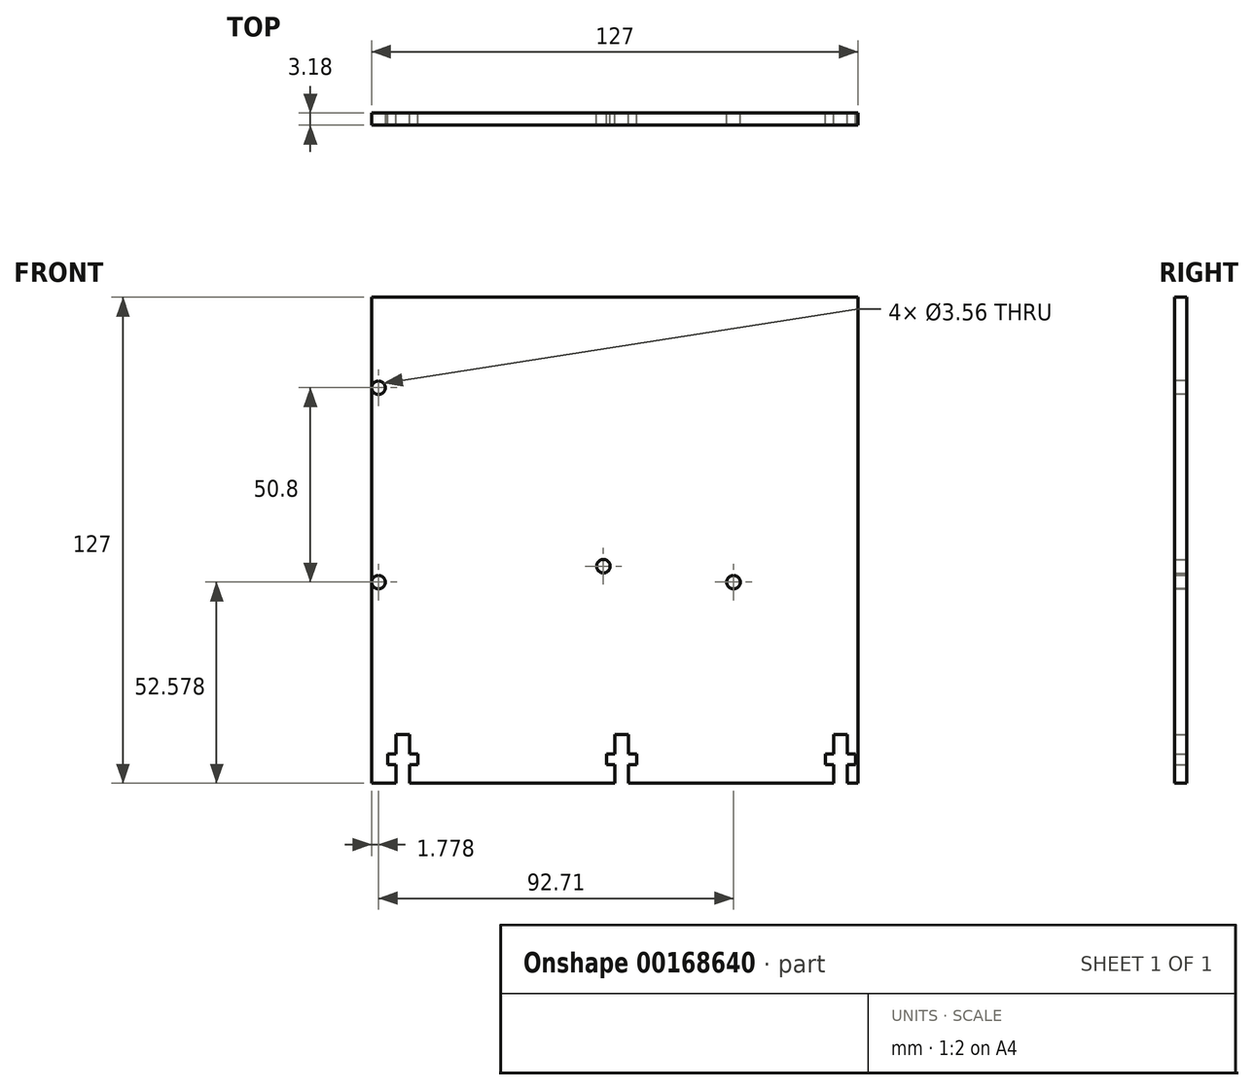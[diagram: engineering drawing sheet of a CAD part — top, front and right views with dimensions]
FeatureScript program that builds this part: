
annotation { "Feature Type Name" : "Feature", "Feature Type Description" : "" }
export const myFeature = defineFeature(function(context is Context, id is Id, definition is map)
    precondition{}
    {
        {
            var Q0;
            Q0=qCreatedBy(makeId("Front.planeOp"),FACE);
            var sketch = newSketch(context, id + "F0", { "sketchPlane" : qUnion([Q0])});
            skLineSegment(sketch, "E0.bottom", {"start": v(63.5, -63.5) * mm, "end": v(-63.5, -63.5) * mm});
            skLineSegment(sketch, "E0.top", {"start": v(63.5, 63.5) * mm, "end": v(-63.5, 63.5) * mm});
            skLineSegment(sketch, "E0.left", {"start": v(63.5, -63.5) * mm, "end": v(63.5, 63.5) * mm});
            skLineSegment(sketch, "E0.right", {"start": v(-63.5, -63.5) * mm, "end": v(-63.5, 63.5) * mm});
            skPoint(sketch, "E0.middle", {"position": v(0, 0) * mm});
            skLineSegment(sketch, "E1", {"start": v(-57.15, -63.5) * mm, "end": v(-57.15, -58.66) * mm});
            skLineSegment(sketch, "E2", {"start": v(-57.15, -58.66) * mm, "end": v(-59.34, -58.66) * mm});
            skLineSegment(sketch, "E3", {"start": v(-59.34, -58.66) * mm, "end": v(-59.34, -55.88) * mm});
            skLineSegment(sketch, "E4", {"start": v(-59.34, -55.88) * mm, "end": v(-57.15, -55.88) * mm});
            skLineSegment(sketch, "E5", {"start": v(-57.15, -55.88) * mm, "end": v(-57.15, -50.8) * mm});
            skLineSegment(sketch, "E6", {"start": v(-57.15, -50.8) * mm, "end": v(-53.6, -50.8) * mm});
            skLineSegment(sketch, "E7", {"start": v(-53.6, -50.8) * mm, "end": v(-53.6, -55.88) * mm});
            skLineSegment(sketch, "E8", {"start": v(-53.6, -55.88) * mm, "end": v(-51.4, -55.88) * mm});
            skLineSegment(sketch, "E9", {"start": v(-51.4, -55.88) * mm, "end": v(-51.4, -58.66) * mm});
            skLineSegment(sketch, "E10", {"start": v(-51.4, -58.66) * mm, "end": v(-53.6, -58.66) * mm});
            skLineSegment(sketch, "E11", {"start": v(-53.6, -58.66) * mm, "end": v(-53.6, -63.5) * mm});
            skLineSegment(sketch, "E12.1.0.0", {"start": v(-2.2, -58.66) * mm, "end": v(-2.2, -55.88) * mm});
            skLineSegment(sketch, "E12.1.0.1", {"start": v(5.75, -58.66) * mm, "end": v(3.56, -58.66) * mm});
            skLineSegment(sketch, "E12.1.0.2", {"start": v(-2.2, -55.88) * mm, "end": v(0, -55.88) * mm});
            skLineSegment(sketch, "E12.1.0.3", {"start": v(0, -55.88) * mm, "end": v(0, -50.8) * mm});
            skLineSegment(sketch, "E12.1.0.4", {"start": v(0, -50.8) * mm, "end": v(3.56, -50.8) * mm});
            skLineSegment(sketch, "E12.1.0.5", {"start": v(0, -58.66) * mm, "end": v(-2.2, -58.66) * mm});
            skLineSegment(sketch, "E12.1.0.6", {"start": v(3.56, -50.8) * mm, "end": v(3.56, -55.88) * mm});
            skLineSegment(sketch, "E12.1.0.7", {"start": v(0, -63.5) * mm, "end": v(0, -58.66) * mm});
            skLineSegment(sketch, "E12.1.0.8", {"start": v(3.56, -55.88) * mm, "end": v(5.75, -55.88) * mm});
            skLineSegment(sketch, "E12.1.0.9", {"start": v(5.75, -55.88) * mm, "end": v(5.75, -58.66) * mm});
            skLineSegment(sketch, "E12.1.0.10", {"start": v(3.56, -58.66) * mm, "end": v(3.56, -63.5) * mm});
            skLineSegment(sketch, "E12.2.0.0", {"start": v(54.96, -58.66) * mm, "end": v(54.96, -55.88) * mm});
            skLineSegment(sketch, "E12.2.0.1", {"start": v(62.9, -58.66) * mm, "end": v(60.7, -58.66) * mm});
            skLineSegment(sketch, "E12.2.0.2", {"start": v(54.96, -55.88) * mm, "end": v(57.15, -55.88) * mm});
            skLineSegment(sketch, "E12.2.0.3", {"start": v(57.15, -55.88) * mm, "end": v(57.15, -50.8) * mm});
            skLineSegment(sketch, "E12.2.0.4", {"start": v(57.15, -50.8) * mm, "end": v(60.7, -50.8) * mm});
            skLineSegment(sketch, "E12.2.0.5", {"start": v(57.15, -58.66) * mm, "end": v(54.96, -58.66) * mm});
            skLineSegment(sketch, "E12.2.0.6", {"start": v(60.7, -50.8) * mm, "end": v(60.7, -55.88) * mm});
            skLineSegment(sketch, "E12.2.0.7", {"start": v(57.15, -63.5) * mm, "end": v(57.15, -58.66) * mm});
            skLineSegment(sketch, "E12.2.0.8", {"start": v(60.7, -55.88) * mm, "end": v(62.9, -55.88) * mm});
            skLineSegment(sketch, "E12.2.0.9", {"start": v(62.9, -55.88) * mm, "end": v(62.9, -58.66) * mm});
            skLineSegment(sketch, "E12.2.0.10", {"start": v(60.7, -58.66) * mm, "end": v(60.7, -63.5) * mm});
            skLineSegment(sketch, "E12.direction1", {"start": v(-57.15, -63.5) * mm, "end": v(0, -63.5) * mm, "construction": true});
            skCircle(sketch, "E13", {"center": v(30.99, -10.92) * mm, "radius": 1.78 * mm});
            skCircle(sketch, "E14", {"center": v(-3, -6.75) * mm, "radius": 1.78 * mm});
            skSolve(sketch);
        }
        {
            var Q0;
            Q0=makeQuery(id+"F0.imprint","IMPRINT",FACE,{"disambiguationData":[TD([[makeQuery(id+"F0.imprint","IMPRINT",EDGE,{"derivedFrom":sQuery(id+"F0.wireOp",EDGE,"E0.top")}),1.0]])]});
            extrude(context, id + "F1", {"entities" : qUnion([Q0]), "endBound" : BoundingType.SYMMETRIC, "depth" : 3.17 * mm});
        }
        {
            var Q0;
            Q0=makeQuery(id+"F1.opExtrude","CAP_FACE",FACE,{"disambiguationData":[OSD([sQuery(id+"F0.wireOp",EDGE,"E0.bottom"),sQuery(id+"F0.wireOp",EDGE,"E0.top"),sQuery(id+"F0.wireOp",EDGE,"E0.left"),sQuery(id+"F0.wireOp",EDGE,"E0.right"),sQuery(id+"F0.wireOp",EDGE,"E1"),sQuery(id+"F0.wireOp",EDGE,"E2"),sQuery(id+"F0.wireOp",EDGE,"E3"),sQuery(id+"F0.wireOp",EDGE,"E4"),sQuery(id+"F0.wireOp",EDGE,"E5"),sQuery(id+"F0.wireOp",EDGE,"E6"),sQuery(id+"F0.wireOp",EDGE,"E7"),sQuery(id+"F0.wireOp",EDGE,"E8"),sQuery(id+"F0.wireOp",EDGE,"E9"),sQuery(id+"F0.wireOp",EDGE,"E10"),sQuery(id+"F0.wireOp",EDGE,"E11"),sQuery(id+"F0.wireOp",EDGE,"E12.1.0.0"),sQuery(id+"F0.wireOp",EDGE,"E12.1.0.1"),sQuery(id+"F0.wireOp",EDGE,"E12.1.0.2"),sQuery(id+"F0.wireOp",EDGE,"E12.1.0.3"),sQuery(id+"F0.wireOp",EDGE,"E12.1.0.4"),sQuery(id+"F0.wireOp",EDGE,"E12.1.0.5"),sQuery(id+"F0.wireOp",EDGE,"E12.1.0.6"),sQuery(id+"F0.wireOp",EDGE,"E12.1.0.7"),sQuery(id+"F0.wireOp",EDGE,"E12.1.0.8"),sQuery(id+"F0.wireOp",EDGE,"E12.1.0.9"),sQuery(id+"F0.wireOp",EDGE,"E12.1.0.10"),sQuery(id+"F0.wireOp",EDGE,"E12.2.0.0"),sQuery(id+"F0.wireOp",EDGE,"E12.2.0.1"),sQuery(id+"F0.wireOp",EDGE,"E12.2.0.2"),sQuery(id+"F0.wireOp",EDGE,"E12.2.0.3"),sQuery(id+"F0.wireOp",EDGE,"E12.2.0.4"),sQuery(id+"F0.wireOp",EDGE,"E12.2.0.5"),sQuery(id+"F0.wireOp",EDGE,"E12.2.0.6"),sQuery(id+"F0.wireOp",EDGE,"E12.2.0.7"),sQuery(id+"F0.wireOp",EDGE,"E12.2.0.8"),sQuery(id+"F0.wireOp",EDGE,"E12.2.0.9"),sQuery(id+"F0.wireOp",EDGE,"E12.2.0.10"),sQuery(id+"F0.wireOp",EDGE,"E13"),sQuery(id+"F0.wireOp",EDGE,"E14")])],"isStart":false});
            var sketch = newSketch(context, id + "F2", { "sketchPlane" : qUnion([Q0])});
            skCircle(sketch, "E15", {"center": v(-61.72, -10.92) * mm, "radius": 1.78 * mm});
            skCircle(sketch, "E16.0.1.0", {"center": v(-61.72, 39.88) * mm, "radius": 1.78 * mm});
            skLineSegment(sketch, "E16.direction1", {"start": v(-61.72, -10.92) * mm, "end": v(-36.32, -10.92) * mm, "construction": true});
            skLineSegment(sketch, "E16.direction2", {"start": v(-61.72, -10.92) * mm, "end": v(-61.72, 39.88) * mm, "construction": true});
            skSolve(sketch);
        }
        {
            var Q0;
            Q0=sQuery(id+"F2.wireOp",VERTEX,"E16.0.1.0.center");
            var Q1;
            Q1=sQuery(id+"F2.wireOp",VERTEX,"E15.center");
            var Q2;
            Q2=makeQuery(id+"F1.opExtrude","SWEPT_BODY",BODY,{"disambiguationData":[OSD([sQuery(id+"F0.wireOp",EDGE,"E0.bottom"),sQuery(id+"F0.wireOp",EDGE,"E0.top"),sQuery(id+"F0.wireOp",EDGE,"E0.left"),sQuery(id+"F0.wireOp",EDGE,"E0.right"),sQuery(id+"F0.wireOp",EDGE,"E1"),sQuery(id+"F0.wireOp",EDGE,"E2"),sQuery(id+"F0.wireOp",EDGE,"E3"),sQuery(id+"F0.wireOp",EDGE,"E4"),sQuery(id+"F0.wireOp",EDGE,"E5"),sQuery(id+"F0.wireOp",EDGE,"E6"),sQuery(id+"F0.wireOp",EDGE,"E7"),sQuery(id+"F0.wireOp",EDGE,"E8"),sQuery(id+"F0.wireOp",EDGE,"E9"),sQuery(id+"F0.wireOp",EDGE,"E10"),sQuery(id+"F0.wireOp",EDGE,"E11"),sQuery(id+"F0.wireOp",EDGE,"E12.1.0.0"),sQuery(id+"F0.wireOp",EDGE,"E12.1.0.1"),sQuery(id+"F0.wireOp",EDGE,"E12.1.0.2"),sQuery(id+"F0.wireOp",EDGE,"E12.1.0.3"),sQuery(id+"F0.wireOp",EDGE,"E12.1.0.4"),sQuery(id+"F0.wireOp",EDGE,"E12.1.0.5"),sQuery(id+"F0.wireOp",EDGE,"E12.1.0.6"),sQuery(id+"F0.wireOp",EDGE,"E12.1.0.7"),sQuery(id+"F0.wireOp",EDGE,"E12.1.0.8"),sQuery(id+"F0.wireOp",EDGE,"E12.1.0.9"),sQuery(id+"F0.wireOp",EDGE,"E12.1.0.10"),sQuery(id+"F0.wireOp",EDGE,"E12.2.0.0"),sQuery(id+"F0.wireOp",EDGE,"E12.2.0.1"),sQuery(id+"F0.wireOp",EDGE,"E12.2.0.2"),sQuery(id+"F0.wireOp",EDGE,"E12.2.0.3"),sQuery(id+"F0.wireOp",EDGE,"E12.2.0.4"),sQuery(id+"F0.wireOp",EDGE,"E12.2.0.5"),sQuery(id+"F0.wireOp",EDGE,"E12.2.0.6"),sQuery(id+"F0.wireOp",EDGE,"E12.2.0.7"),sQuery(id+"F0.wireOp",EDGE,"E12.2.0.8"),sQuery(id+"F0.wireOp",EDGE,"E12.2.0.9"),sQuery(id+"F0.wireOp",EDGE,"E12.2.0.10"),sQuery(id+"F0.wireOp",EDGE,"E13"),sQuery(id+"F0.wireOp",EDGE,"E14")])]});
            hole(context, id + "F3", {"style" : HoleStyle.SIMPLE, "endStyle" : HoleEndStyle.THROUGH, "holeDiameter" : 3.56 * mm, "locations" : qUnion([Q0, Q1]), "scope" : qUnion([Q2]), "isTappedThrough" : true});
        }
    });
